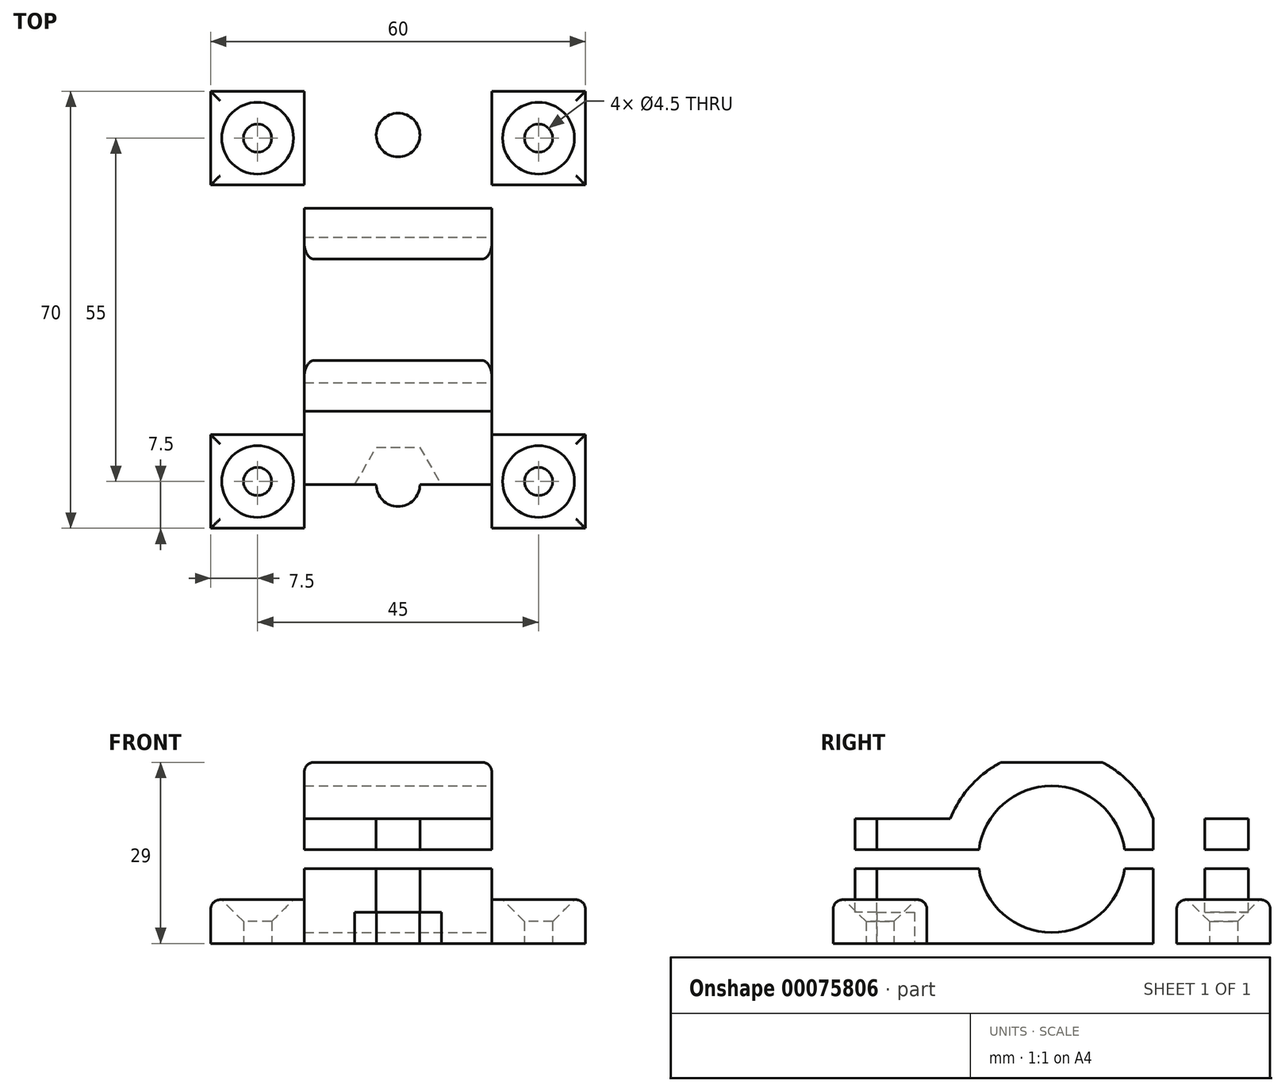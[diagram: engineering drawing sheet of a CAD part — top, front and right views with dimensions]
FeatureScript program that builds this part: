
annotation { "Feature Type Name" : "Feature", "Feature Type Description" : "" }
export const myFeature = defineFeature(function(context is Context, id is Id, definition is map)
    precondition{}
    {
        {
            var Q0;
            Q0=qCreatedBy(makeId("Top.planeOp"),FACE);
            var sketch = newSketch(context, id + "F0", { "sketchPlane" : qUnion([Q0])});
            skLineSegment(sketch, "E0.bottom", {"start": v(15, 35) * mm, "end": v(-15, 35) * mm});
            skLineSegment(sketch, "E0.top", {"start": v(15, -35) * mm, "end": v(-15, -35) * mm});
            skLineSegment(sketch, "E0.left", {"start": v(15, 35) * mm, "end": v(15, -35) * mm});
            skLineSegment(sketch, "E0.right", {"start": v(-15, 35) * mm, "end": v(-15, -35) * mm});
            skPoint(sketch, "E0.middle", {"position": v(0, 0) * mm});
            skSolve(sketch);
        }
        {
            var Q0;
            Q0=makeQuery(id+"F0.imprint","IMPRINT",FACE,{"disambiguationData":[TD([[makeQuery(id+"F0.imprint","IMPRINT",EDGE,{"derivedFrom":sQuery(id+"F0.wireOp",EDGE,"E0.bottom")}),1.0]])]});
            extrude(context, id + "F1", {"entities" : qUnion([Q0]), "depth" : 12 * mm});
        }
        {
            var Q0;
            Q0=qCreatedBy(makeId("Right.planeOp"),FACE);
            var sketch = newSketch(context, id + "F2", { "sketchPlane" : qUnion([Q0])});
            skLineSegment(sketch, "E1.bottom", {"start": v(-35, 15) * mm, "end": v(35, 15) * mm});
            skLineSegment(sketch, "E1.top", {"start": v(-35, 12) * mm, "end": v(35, 12) * mm});
            skLineSegment(sketch, "E1.left", {"start": v(-35, 15) * mm, "end": v(-35, 12) * mm});
            skLineSegment(sketch, "E1.right", {"start": v(35, 15) * mm, "end": v(35, 12) * mm});
            skLineSegment(sketch, "E2.bottom", {"start": v(-35, 29) * mm, "end": v(35, 29) * mm});
            skLineSegment(sketch, "E2.left", {"start": v(-35, 29) * mm, "end": v(-35, 15) * mm});
            skLineSegment(sketch, "E2.right", {"start": v(35, 29) * mm, "end": v(35, 15) * mm});
            skSolve(sketch);
        }
        {
            var Q0;
            Q0=makeQuery(id+"F2.imprint","IMPRINT",FACE,{"disambiguationData":[TD([[makeQuery(id+"F2.imprint","IMPRINT",EDGE,{"derivedFrom":sQuery(id+"F2.wireOp",EDGE,"E2.bottom")}),-1.0]])]});
            extrude(context, id + "F3", {"entities" : qUnion([Q0]), "endBound" : BoundingType.SYMMETRIC, "depth" : 30 * mm});
        }
        {
            var Q0;
            Q0=qCreatedBy(makeId("Right.planeOp"),FACE);
            var sketch = newSketch(context, id + "F4", { "sketchPlane" : qUnion([Q0])});
            skLineSegment(sketch, "E3.bottom", {"start": v(-35, 13.5) * mm, "end": v(0, 13.5) * mm});
            skLineSegment(sketch, "E3.top", {"start": v(-35, 12) * mm, "end": v(0, 12) * mm});
            skLineSegment(sketch, "E3.left", {"start": v(-35, 13.5) * mm, "end": v(-35, 12) * mm});
            skLineSegment(sketch, "E3.right", {"start": v(0, 13.5) * mm, "end": v(0, 12) * mm});
            skCircle(sketch, "E4", {"center": v(0, 13.5) * mm, "radius": 11.75 * mm});
            skSolve(sketch);
        }
        {
            var Q0;
            {var subQ0=sQuery(id+"F4.wireOp",EDGE,"E3.right");Q0=makeQuery(id+"F4.imprint","IMPRINT",FACE,{"disambiguationData":[TD([[makeQuery(id+"F4.imprint","IMPRINT",EDGE,{"derivedFrom":subQ0}),1.0]])]});}
            var Q1;
            {var subQ0=sQuery(id+"F4.wireOp",EDGE,"E3.right");Q1=makeQuery(id+"F4.imprint","IMPRINT",FACE,{"disambiguationData":[TD([[makeQuery(id+"F4.imprint","IMPRINT",EDGE,{"derivedFrom":subQ0}),-1.0]])]});}
            extrude(context, id + "F5", {"entities" : qUnion([Q0, Q1]), "operationType" : NewBodyOperationType.REMOVE, "endBound" : BoundingType.SYMMETRIC, "oppositeDirection" : true, "depth" : 30 * mm});
        }
        {
            var Q0;
            Q0=qCreatedBy(makeId("Right.planeOp"),FACE);
            var sketch = newSketch(context, id + "F6", { "sketchPlane" : qUnion([Q0])});
            skArc(sketch, "E5", {"start": v(-8.12, 29) * mm, "mid": v(-13, 25.23) * mm, "end": v(-16.25, 20) * mm});
            skLineSegment(sketch, "E6.bottom", {"start": v(-35, 29) * mm, "end": v(-8.12, 29) * mm});
            skLineSegment(sketch, "E6.left", {"start": v(-35, 29) * mm, "end": v(-35, 20) * mm});
            skLineSegment(sketch, "E6.right", {"start": v(35, 29) * mm, "end": v(35, 20) * mm});
            skArc(sketch, "E7.trimOffspring", {"start": v(16.25, 20) * mm, "mid": v(13, 25.23) * mm, "end": v(8.12, 29) * mm});
            skLineSegment(sketch, "E8.trimOffspring", {"start": v(8.12, 29) * mm, "end": v(35, 29) * mm});
            skLineSegment(sketch, "E9.top", {"start": v(-35, 20) * mm, "end": v(-16.25, 20) * mm});
            skPoint(sketch, "E9.left.start.orphan", {"position": v(-35, 15) * mm});
            skLineSegment(sketch, "E10.top", {"start": v(35, 20) * mm, "end": v(16.25, 20) * mm});
            skPoint(sketch, "E10.left.start.orphan", {"position": v(35, 15) * mm});
            skSolve(sketch);
        }
        {
            var Q0;
            Q0=makeQuery(id+"F6.imprint","IMPRINT",FACE,{"disambiguationData":[TD([[makeQuery(id+"F6.imprint","IMPRINT",EDGE,{"derivedFrom":sQuery(id+"F6.wireOp",EDGE,"E5")}),-1.0]])]});
            var Q1;
            Q1=makeQuery(id+"F6.imprint","IMPRINT",FACE,{"disambiguationData":[TD([[makeQuery(id+"F6.imprint","IMPRINT",EDGE,{"derivedFrom":sQuery(id+"F6.wireOp",EDGE,"E6.right")}),-1.0]])]});
            extrude(context, id + "F7", {"entities" : qUnion([Q0, Q1]), "operationType" : NewBodyOperationType.REMOVE, "endBound" : BoundingType.SYMMETRIC, "oppositeDirection" : true, "depth" : 30 * mm});
        }
        {
            var Q0;
            Q0=makeQuery(id+"F7.boolean.opBoolean","COPY",FACE,{"derivedFrom":makeQuery(id+"F7.opExtrude","SWEPT_FACE",FACE,{"disambiguationData":[OSD([sQuery(id+"F6.wireOp",EDGE,"E10.top")])]})});
            var sketch = newSketch(context, id + "F8", { "sketchPlane" : qUnion([Q0])});
            skLineSegment(sketch, "E11.bottom", {"start": v(-15, 35) * mm, "end": v(15, 35) * mm});
            skLineSegment(sketch, "E11.top", {"start": v(-15, 28) * mm, "end": v(15, 28) * mm});
            skLineSegment(sketch, "E11.left", {"start": v(-15, 35) * mm, "end": v(-15, 28) * mm});
            skLineSegment(sketch, "E11.right", {"start": v(15, 35) * mm, "end": v(15, 28) * mm});
            skCircle(sketch, "E12", {"center": v(0, 28) * mm, "radius": 3.5 * mm});
            skLineSegment(sketch, "E13.bottom", {"start": v(-15, -35) * mm, "end": v(15, -35) * mm});
            skLineSegment(sketch, "E13.top", {"start": v(-15, -28) * mm, "end": v(15, -28) * mm});
            skLineSegment(sketch, "E13.left", {"start": v(-15, -35) * mm, "end": v(-15, -28) * mm});
            skLineSegment(sketch, "E13.right", {"start": v(15, -35) * mm, "end": v(15, -28) * mm});
            skCircle(sketch, "E14", {"center": v(0, -28) * mm, "radius": 3.5 * mm});
            skSolve(sketch);
        }
        {
            var Q0;
            {var subQ0=sQuery(id+"F8.wireOp",EDGE,"E12");var subQ1=sQuery(id+"F8.wireOp",EDGE,"E11.top");var subQ2=makeQuery(id+"F8.imprint","INTERSECT",VERTEX,{"disambiguationData":[OD(0.0)],"derivedFrom":[subQ1,subQ0]});Q0=makeQuery(id+"F8.imprint","IMPRINT",FACE,{"disambiguationData":[TD([[makeQuery(id+"F8.imprint","IMPRINT",EDGE,{"disambiguationData":[TD([[subQ2,-1.0]])],"derivedFrom":subQ1}),-1.0]])]});}
            var Q1;
            {var subQ0=sQuery(id+"F8.wireOp",EDGE,"E14");var subQ1=sQuery(id+"F8.wireOp",EDGE,"E13.top");var subQ2=makeQuery(id+"F8.imprint","INTERSECT",VERTEX,{"disambiguationData":[OD(0.0)],"derivedFrom":[subQ1,subQ0]});Q1=makeQuery(id+"F8.imprint","IMPRINT",FACE,{"disambiguationData":[TD([[makeQuery(id+"F8.imprint","IMPRINT",EDGE,{"disambiguationData":[TD([[subQ2,-1.0]])],"derivedFrom":subQ1}),-1.0]])]});}
            var Q2;
            {var subQ0=sQuery(id+"F8.wireOp",EDGE,"E14");var subQ1=sQuery(id+"F8.wireOp",EDGE,"E13.top");var subQ2=makeQuery(id+"F8.imprint","INTERSECT",VERTEX,{"disambiguationData":[OD(0.0)],"derivedFrom":[subQ1,subQ0]});Q2=makeQuery(id+"F8.imprint","IMPRINT",FACE,{"disambiguationData":[TD([[makeQuery(id+"F8.imprint","IMPRINT",EDGE,{"disambiguationData":[TD([[subQ2,-1.0]])],"derivedFrom":subQ1}),1.0]])]});}
            var Q3;
            {var subQ0=sQuery(id+"F8.wireOp",EDGE,"E12");var subQ1=sQuery(id+"F8.wireOp",EDGE,"E11.top");var subQ2=makeQuery(id+"F8.imprint","INTERSECT",VERTEX,{"disambiguationData":[OD(0.0)],"derivedFrom":[subQ1,subQ0]});Q3=makeQuery(id+"F8.imprint","IMPRINT",FACE,{"disambiguationData":[TD([[makeQuery(id+"F8.imprint","IMPRINT",EDGE,{"disambiguationData":[TD([[subQ2,-1.0]])],"derivedFrom":subQ1}),1.0]])]});}
            extrude(context, id + "F9", {"entities" : qUnion([Q0, Q1, Q2, Q3]), "operationType" : NewBodyOperationType.REMOVE, "endBound" : BoundingType.THROUGH_ALL, "oppositeDirection" : true, "depth" : 25 * mm});
        }
        {
            var Q0;
            Q0=qCreatedBy(makeId("Top.planeOp"),FACE);
            var sketch = newSketch(context, id + "F10", { "sketchPlane" : qUnion([Q0])});
            skCircle(sketch, "E15.cCircle", {"center": v(0, -28) * mm, "radius": 6 * mm, "construction": true});
            skLineSegment(sketch, "E15.0", {"start": v(-3.46, -22) * mm, "end": v(3.46, -22) * mm});
            skLineSegment(sketch, "E15.1", {"start": v(3.46, -22) * mm, "end": v(6.93, -28) * mm});
            skLineSegment(sketch, "E15.2", {"start": v(6.93, -28) * mm, "end": v(3.46, -34) * mm});
            skLineSegment(sketch, "E15.3", {"start": v(3.46, -34) * mm, "end": v(-3.46, -34) * mm});
            skLineSegment(sketch, "E15.4", {"start": v(-3.46, -34) * mm, "end": v(-6.93, -28) * mm});
            skLineSegment(sketch, "E15.5", {"start": v(-6.93, -28) * mm, "end": v(-3.46, -22) * mm});
            skPoint(sketch, "E15.0.midPoint", {"position": v(0, -22) * mm});
            skCircle(sketch, "E16.cCircle", {"center": v(0, 27.96) * mm, "radius": 6 * mm, "construction": true});
            skLineSegment(sketch, "E16.0", {"start": v(6.93, 27.96) * mm, "end": v(3.46, 21.96) * mm});
            skLineSegment(sketch, "E16.1", {"start": v(3.46, 21.96) * mm, "end": v(-3.46, 21.96) * mm});
            skLineSegment(sketch, "E16.2", {"start": v(-3.46, 21.96) * mm, "end": v(-6.93, 27.96) * mm});
            skLineSegment(sketch, "E16.3", {"start": v(-6.93, 27.96) * mm, "end": v(-3.46, 33.96) * mm});
            skLineSegment(sketch, "E16.4", {"start": v(-3.46, 33.96) * mm, "end": v(3.46, 33.96) * mm});
            skLineSegment(sketch, "E16.5", {"start": v(3.46, 33.96) * mm, "end": v(6.93, 27.96) * mm});
            skPoint(sketch, "E16.0.midPoint", {"position": v(5.2, 24.96) * mm});
            skSolve(sketch);
        }
        {
            var Q0;
            Q0=makeQuery(id+"F10.imprint","IMPRINT",FACE,{"disambiguationData":[TD([[makeQuery(id+"F10.imprint","IMPRINT",EDGE,{"derivedFrom":sQuery(id+"F10.wireOp",EDGE,"E15.0")}),-1.0]])]});
            var Q1;
            Q1=makeQuery(id+"F10.imprint","IMPRINT",FACE,{"disambiguationData":[TD([[makeQuery(id+"F10.imprint","IMPRINT",EDGE,{"derivedFrom":sQuery(id+"F10.wireOp",EDGE,"E16.0")}),-1.0]])]});
            extrude(context, id + "F11", {"entities" : qUnion([Q0, Q1]), "operationType" : NewBodyOperationType.REMOVE, "depth" : 5 * mm});
        }
        {
            var Q0;
            Q0=qCreatedBy(makeId("Top.planeOp"),FACE);
            var sketch = newSketch(context, id + "F12", { "sketchPlane" : qUnion([Q0])});
            skLineSegment(sketch, "E17.bottom", {"start": v(-30, -35) * mm, "end": v(-15, -35) * mm});
            skLineSegment(sketch, "E17.top", {"start": v(-30, -20) * mm, "end": v(-15, -20) * mm});
            skLineSegment(sketch, "E17.left", {"start": v(-30, -35) * mm, "end": v(-30, -20) * mm});
            skLineSegment(sketch, "E17.right", {"start": v(-15, -35) * mm, "end": v(-15, -20) * mm});
            skLineSegment(sketch, "E18.MirrorCS", {"start": v(30, -35) * mm, "end": v(15, -35) * mm});
            skLineSegment(sketch, "E19.MirrorCS", {"start": v(15, -35) * mm, "end": v(15, -20) * mm});
            skLineSegment(sketch, "E20.MirrorCS", {"start": v(30, -20) * mm, "end": v(15, -20) * mm});
            skLineSegment(sketch, "E21.MirrorCS", {"start": v(30, -35) * mm, "end": v(30, -20) * mm});
            skLineSegment(sketch, "E22.MirrorCS", {"start": v(-30, 20) * mm, "end": v(-15, 20) * mm});
            skLineSegment(sketch, "E23.MirrorCS", {"start": v(-30, 35) * mm, "end": v(-30, 20) * mm});
            skLineSegment(sketch, "E24.MirrorCS", {"start": v(-30, 35) * mm, "end": v(-15, 35) * mm});
            skLineSegment(sketch, "E25.MirrorCS", {"start": v(-15, 35) * mm, "end": v(-15, 20) * mm});
            skLineSegment(sketch, "E26.MirrorCS", {"start": v(15, 35) * mm, "end": v(15, 20) * mm});
            skLineSegment(sketch, "E27.MirrorCS", {"start": v(30, 20) * mm, "end": v(15, 20) * mm});
            skLineSegment(sketch, "E28.MirrorCS", {"start": v(30, 35) * mm, "end": v(15, 35) * mm});
            skLineSegment(sketch, "E29.MirrorCS", {"start": v(30, 35) * mm, "end": v(30, 20) * mm});
            skCircle(sketch, "E30", {"center": v(-22.5, -27.5) * mm, "radius": 2.25 * mm});
            skCircle(sketch, "E31.MirrorC", {"center": v(22.5, -27.5) * mm, "radius": 2.25 * mm});
            skCircle(sketch, "E32.MirrorC", {"center": v(-22.5, 27.5) * mm, "radius": 2.25 * mm});
            skCircle(sketch, "E33.MirrorC", {"center": v(22.5, 27.5) * mm, "radius": 2.25 * mm});
            skSolve(sketch);
        }
        {
            var Q0;
            Q0=makeQuery(id+"F12.imprint","IMPRINT",FACE,{"disambiguationData":[TD([[makeQuery(id+"F12.imprint","IMPRINT",EDGE,{"derivedFrom":sQuery(id+"F12.wireOp",EDGE,"E22.MirrorCS")}),1.0]])]});
            var Q1;
            Q1=makeQuery(id+"F12.imprint","IMPRINT",FACE,{"disambiguationData":[TD([[makeQuery(id+"F12.imprint","IMPRINT",EDGE,{"derivedFrom":sQuery(id+"F12.wireOp",EDGE,"E17.bottom")}),1.0]])]});
            var Q2;
            Q2=makeQuery(id+"F12.imprint","IMPRINT",FACE,{"disambiguationData":[TD([[makeQuery(id+"F12.imprint","IMPRINT",EDGE,{"derivedFrom":sQuery(id+"F12.wireOp",EDGE,"E18.MirrorCS")}),-1.0]])]});
            var Q3;
            Q3=makeQuery(id+"F12.imprint","IMPRINT",FACE,{"disambiguationData":[TD([[makeQuery(id+"F12.imprint","IMPRINT",EDGE,{"derivedFrom":sQuery(id+"F12.wireOp",EDGE,"E27.MirrorCS")}),-1.0]])]});
            extrude(context, id + "F13", {"entities" : qUnion([Q0, Q1, Q2, Q3]), "operationType" : NewBodyOperationType.ADD, "depth" : 7 * mm});
        }
        {
            var Q0;
            Q0=makeQuery(id+"F13.opExtrude","CAP_EDGE",EDGE,{"disambiguationData":[OSD([sQuery(id+"F12.wireOp",EDGE,"E32.MirrorC")])],"isStart":false});
            var Q1;
            Q1=makeQuery(id+"F13.opExtrude","CAP_EDGE",EDGE,{"disambiguationData":[OSD([sQuery(id+"F12.wireOp",EDGE,"E33.MirrorC")])],"isStart":false});
            var Q2;
            Q2=makeQuery(id+"F13.opExtrude","CAP_EDGE",EDGE,{"disambiguationData":[OSD([sQuery(id+"F12.wireOp",EDGE,"E31.MirrorC")])],"isStart":false});
            var Q3;
            Q3=makeQuery(id+"F13.opExtrude","CAP_EDGE",EDGE,{"disambiguationData":[OSD([sQuery(id+"F12.wireOp",EDGE,"E30")])],"isStart":false});
            chamfer(context, id + "F14", {"entities" : qUnion([Q0, Q1, Q2, Q3]), "width" : 3.5 * mm, "tangentPropagation" : true});
        }
        {
            var Q0;
            Q0=makeQuery(id+"F7.boolean.opBoolean","COPY",EDGE,{"derivedFrom":makeQuery(id+"F7.opExtrude","CAP_EDGE",EDGE,{"disambiguationData":[OSD([sQuery(id+"F6.wireOp",EDGE,"E10.top")])],"isStart":false})});
            var Q1;
            Q1=makeQuery(id+"F7.boolean.opBoolean","COPY",EDGE,{"derivedFrom":makeQuery(id+"F7.opExtrude","SWEPT_EDGE",EDGE,{"disambiguationData":[OSD([sQuery(id+"F6.wireOp",EDGE,"E6.right"),sQuery(id+"F6.wireOp",EDGE,"E10.top")])]})});
            var Q2;
            Q2=makeQuery(id+"F7.boolean.opBoolean","COPY",EDGE,{"derivedFrom":makeQuery(id+"F7.opExtrude","CAP_EDGE",EDGE,{"disambiguationData":[OSD([sQuery(id+"F6.wireOp",EDGE,"E10.top")])],"isStart":true})});
            var Q3;
            Q3=makeQuery(id+"F7.boolean.opBoolean","COPY",EDGE,{"derivedFrom":makeQuery(id+"F7.opExtrude","CAP_EDGE",EDGE,{"disambiguationData":[OSD([sQuery(id+"F6.wireOp",EDGE,"E7.trimOffspring")])],"isStart":true})});
            var Q4;
            Q4=makeQuery(id+"F7.boolean.opBoolean","COPY",EDGE,{"derivedFrom":makeQuery(id+"F7.opExtrude","CAP_EDGE",EDGE,{"disambiguationData":[OSD([sQuery(id+"F6.wireOp",EDGE,"E7.trimOffspring")])],"isStart":false})});
            var Q5;
            Q5=makeQuery(id+"F3.opExtrude","CAP_EDGE",EDGE,{"disambiguationData":[OSD([sQuery(id+"F2.wireOp",EDGE,"E2.bottom")])],"isStart":true});
            var Q6;
            Q6=makeQuery(id+"F3.opExtrude","CAP_EDGE",EDGE,{"disambiguationData":[OSD([sQuery(id+"F2.wireOp",EDGE,"E2.bottom")])],"isStart":false});
            var Q7;
            Q7=makeQuery(id+"F7.boolean.opBoolean","COPY",EDGE,{"derivedFrom":makeQuery(id+"F7.opExtrude","CAP_EDGE",EDGE,{"disambiguationData":[OSD([sQuery(id+"F6.wireOp",EDGE,"E5")])],"isStart":true})});
            var Q8;
            Q8=makeQuery(id+"F7.boolean.opBoolean","COPY",EDGE,{"derivedFrom":makeQuery(id+"F7.opExtrude","CAP_EDGE",EDGE,{"disambiguationData":[OSD([sQuery(id+"F6.wireOp",EDGE,"E5")])],"isStart":false})});
            var Q9;
            Q9=makeQuery(id+"F7.boolean.opBoolean","COPY",EDGE,{"derivedFrom":makeQuery(id+"F7.opExtrude","CAP_EDGE",EDGE,{"disambiguationData":[OSD([sQuery(id+"F6.wireOp",EDGE,"E9.top")])],"isStart":false})});
            var Q10;
            Q10=makeQuery(id+"F7.boolean.opBoolean","COPY",EDGE,{"derivedFrom":makeQuery(id+"F7.opExtrude","SWEPT_EDGE",EDGE,{"disambiguationData":[OSD([sQuery(id+"F6.wireOp",EDGE,"E6.left"),sQuery(id+"F6.wireOp",EDGE,"E9.top")])]})});
            var Q11;
            Q11=makeQuery(id+"F7.boolean.opBoolean","COPY",EDGE,{"derivedFrom":makeQuery(id+"F7.opExtrude","CAP_EDGE",EDGE,{"disambiguationData":[OSD([sQuery(id+"F6.wireOp",EDGE,"E9.top")])],"isStart":true})});
            var Q12;
            Q12=makeQuery(id+"F13.opExtrude","CAP_EDGE",EDGE,{"disambiguationData":[OSD([sQuery(id+"F12.wireOp",EDGE,"E17.bottom")])],"isStart":false});
            var Q13;
            Q13=makeQuery(id+"F13.opExtrude","CAP_EDGE",EDGE,{"disambiguationData":[OSD([sQuery(id+"F12.wireOp",EDGE,"E17.left")])],"isStart":false});
            var Q14;
            Q14=makeQuery(id+"F13.opExtrude","CAP_EDGE",EDGE,{"disambiguationData":[OSD([sQuery(id+"F12.wireOp",EDGE,"E17.top")])],"isStart":false});
            var Q15;
            Q15=makeQuery(id+"F13.opExtrude","CAP_EDGE",EDGE,{"disambiguationData":[OSD([sQuery(id+"F12.wireOp",EDGE,"E18.MirrorCS")])],"isStart":false});
            var Q16;
            Q16=makeQuery(id+"F13.opExtrude","CAP_EDGE",EDGE,{"disambiguationData":[OSD([sQuery(id+"F12.wireOp",EDGE,"E21.MirrorCS")])],"isStart":false});
            var Q17;
            Q17=makeQuery(id+"F13.opExtrude","CAP_EDGE",EDGE,{"disambiguationData":[OSD([sQuery(id+"F12.wireOp",EDGE,"E20.MirrorCS")])],"isStart":false});
            var Q18;
            Q18=makeQuery(id+"F13.opExtrude","CAP_EDGE",EDGE,{"disambiguationData":[OSD([sQuery(id+"F12.wireOp",EDGE,"E27.MirrorCS")])],"isStart":false});
            var Q19;
            Q19=makeQuery(id+"F13.opExtrude","CAP_EDGE",EDGE,{"disambiguationData":[OSD([sQuery(id+"F12.wireOp",EDGE,"E29.MirrorCS")])],"isStart":false});
            var Q20;
            Q20=makeQuery(id+"F13.opExtrude","CAP_EDGE",EDGE,{"disambiguationData":[OSD([sQuery(id+"F12.wireOp",EDGE,"E28.MirrorCS")])],"isStart":false});
            var Q21;
            Q21=makeQuery(id+"F13.opExtrude","CAP_EDGE",EDGE,{"disambiguationData":[OSD([sQuery(id+"F12.wireOp",EDGE,"E24.MirrorCS")])],"isStart":false});
            var Q22;
            Q22=makeQuery(id+"F13.opExtrude","CAP_EDGE",EDGE,{"disambiguationData":[OSD([sQuery(id+"F12.wireOp",EDGE,"E23.MirrorCS")])],"isStart":false});
            var Q23;
            Q23=makeQuery(id+"F13.opExtrude","CAP_EDGE",EDGE,{"disambiguationData":[OSD([sQuery(id+"F12.wireOp",EDGE,"E22.MirrorCS")])],"isStart":false});
            var Q24;
            Q24=makeQuery(id+"F7.boolean.opBoolean","COPY",EDGE,{"derivedFrom":makeQuery(id+"F7.opExtrude","SWEPT_EDGE",EDGE,{"disambiguationData":[OSD([sQuery(id+"F6.wireOp",EDGE,"E5"),sQuery(id+"F6.wireOp",EDGE,"E6.bottom")])]})});
            var Q25;
            Q25=makeQuery(id+"F7.boolean.opBoolean","COPY",EDGE,{"derivedFrom":makeQuery(id+"F7.opExtrude","SWEPT_EDGE",EDGE,{"disambiguationData":[OSD([sQuery(id+"F6.wireOp",EDGE,"E7.trimOffspring"),sQuery(id+"F6.wireOp",EDGE,"E8.trimOffspring")])]})});
            fillet(context, id + "F15", {"entities" : qUnion([Q0, Q1, Q2, Q3, Q4, Q5, Q6, Q7, Q8, Q9, Q10, Q11, Q12, Q13, Q14, Q15, Q16, Q17, Q18, Q19, Q20, Q21, Q22, Q23, Q24, Q25]), "radius" : 1.5 * mm, "tangentPropagation" : true, "allowEdgeOverflow" : false});
        }
    });
